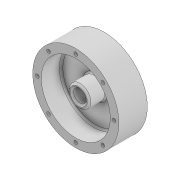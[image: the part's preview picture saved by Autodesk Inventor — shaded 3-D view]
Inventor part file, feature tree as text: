
AUTODESK INVENTOR PART (.ipt)
format: ipt  version: 2020.3 (Build 243373010, 373A)  size: 175,104 bytes
history: native  units: mm
features: sketch x5, extrude x4, chamfer x2, hole x1, pattern_circular x1, fillet x1, projected_geometry x1
ambient origin geometry x8: Origin, YZ Plane, XZ Plane, XY Plane, X Axis, Y Axis, Z Axis, Center Point
bodies: Solid1 (feature_tree)
feature tree (15):
  sketch  "Sketch1"  dims[d1=10.0mm d2=0.0mm d20=80.0mm]
  extrude  "Extrusion1"  Depth=10.0mm
  extrude  "Extrusion4"  Depth=2.0mm TaperAngle=360.0deg
  hole  "Hole2"  [1 undecoded]
  pattern_circular  "Circular Pattern2"  Count=2  [1 undecoded]
  extrude  "Extrusion5"  Depth=2.0mm TaperAngle=45.0deg
  sketch  "Sketch6"  dims[d34=15.0mm d35=0.0mm d36=0.0mm]
  extrude  "Extrusion7"  Depth=2.0mm
  chamfer  "Chamfer1"  Distance=2.0mm Angle=45.0deg
  fillet  "Fillet1"  [1 undecoded]
  chamfer  "Chamfer2"  [1 undecoded]
  sketch  "Sketch4"  dims[d21=23.0mm d22=0.0mm]
  sketch  "Sketch5"  dims[d23=4.134mm d24=10.0mm d25=7.0mm d26=2.0mm d27=90.0deg d28=14.2mm d29=20.594885mm d30=80.0mm d31=360.0deg]
  projected_geometry  "Projected Loop1"
  sketch  "Sketch8"  dims[d50=25.0mm d51=20.0mm d52=0.0mm d53=2.0mm d54=2.0mm d55=45.0deg d56=2.0mm d57=2.0mm d58=2.0mm d59=45.0deg]
note: 4 required parameter values undecoded (feature->parameter linkage not recoverable at this tier; creation-order binding heuristic only, values carry confidence <= 0.55)
